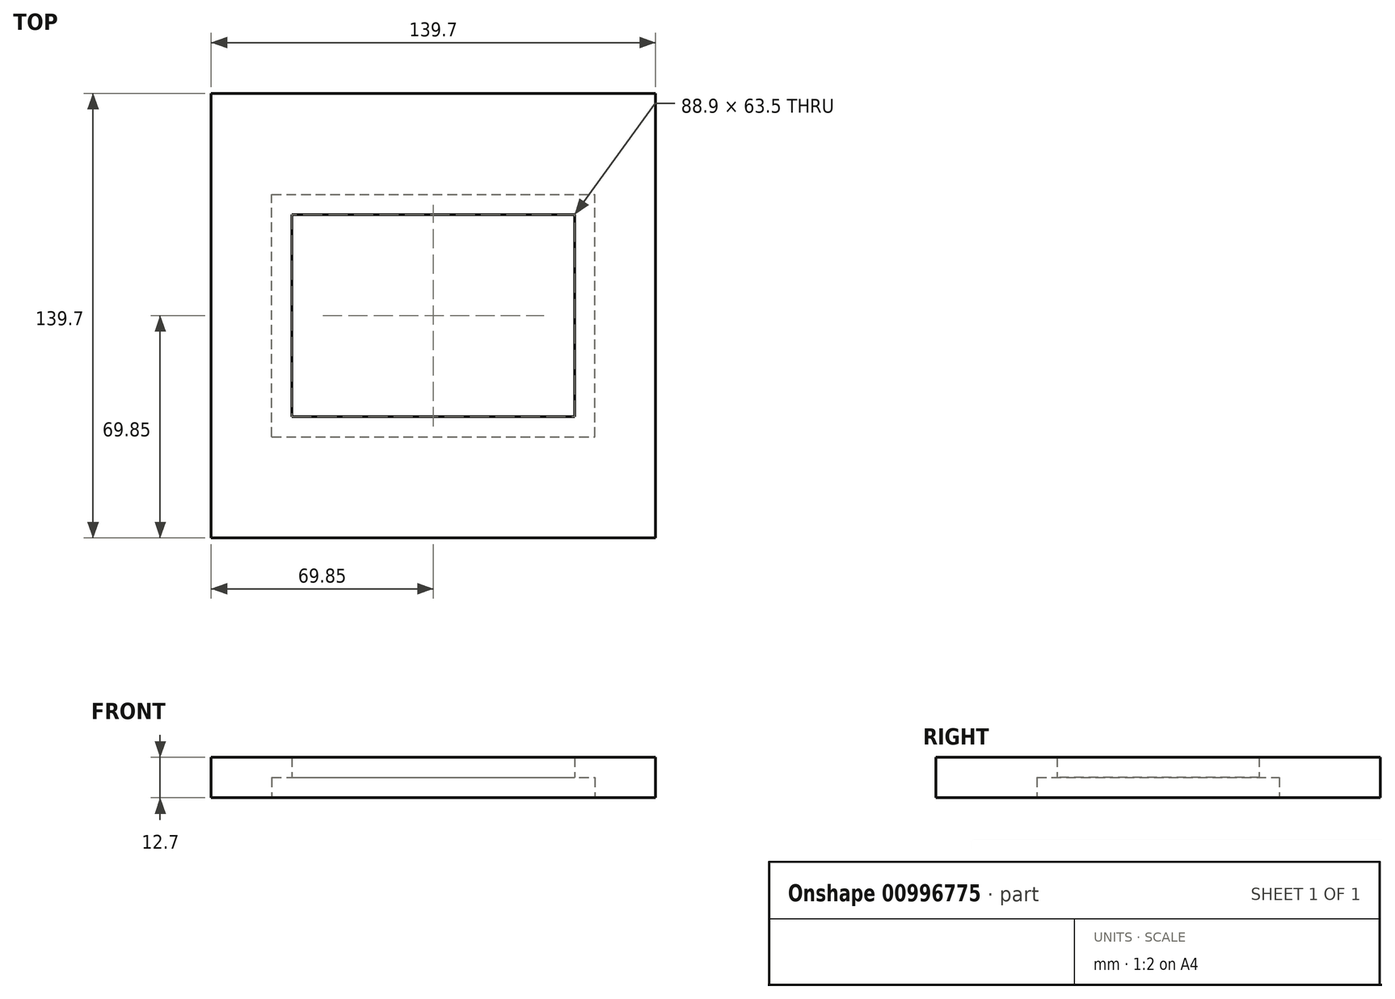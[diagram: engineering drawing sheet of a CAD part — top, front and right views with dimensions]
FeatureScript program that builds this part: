
annotation { "Feature Type Name" : "Feature", "Feature Type Description" : "" }
export const myFeature = defineFeature(function(context is Context, id is Id, definition is map)
    precondition{}
    {
        {
            var Q0;
            Q0=qCreatedBy(makeId("Top.planeOp"),FACE);
            var sketch = newSketch(context, id + "F0", { "sketchPlane" : qUnion([Q0])});
            skLineSegment(sketch, "E0.bottom", {"start": v(-50.8, -38.1) * mm, "end": v(50.8, -38.1) * mm});
            skLineSegment(sketch, "E0.top", {"start": v(-50.8, 38.1) * mm, "end": v(50.8, 38.1) * mm});
            skLineSegment(sketch, "E0.left", {"start": v(-50.8, -38.1) * mm, "end": v(-50.8, 38.1) * mm});
            skLineSegment(sketch, "E0.right", {"start": v(50.8, -38.1) * mm, "end": v(50.8, 38.1) * mm});
            skLineSegment(sketch, "E1", {"start": v(-50.8, 0) * mm, "end": v(50.8, 0) * mm, "construction": true});
            skLineSegment(sketch, "E2", {"start": v(0, 38.1) * mm, "end": v(0, -38.1) * mm, "construction": true});
            skSolve(sketch);
        }
        {
            var Q0;
            Q0=qCreatedBy(makeId("Top.planeOp"),FACE);
            var sketch = newSketch(context, id + "F1", { "sketchPlane" : qUnion([Q0])});
            skLineSegment(sketch, "E3.bottom", {"start": v(-95.25, 95.25) * mm, "end": v(95.25, 95.25) * mm});
            skLineSegment(sketch, "E3.top", {"start": v(-95.25, -95.25) * mm, "end": v(95.25, -95.25) * mm});
            skLineSegment(sketch, "E3.left", {"start": v(-95.25, 95.25) * mm, "end": v(-95.25, -95.25) * mm});
            skLineSegment(sketch, "E3.right", {"start": v(95.25, 95.25) * mm, "end": v(95.25, -95.25) * mm});
            skPoint(sketch, "E3.middle", {"position": v(0, 0) * mm});
            skSolve(sketch);
        }
        {
            var Q0;
            Q0=makeQuery(id+"F1.imprint","IMPRINT",FACE,{"disambiguationData":[TD([[makeQuery(id+"F1.imprint","IMPRINT",EDGE,{"derivedFrom":sQuery(id+"F1.wireOp",EDGE,"E3.bottom")}),-1.0]])]});
            var sketch = newSketch(context, id + "F2", { "sketchPlane" : qUnion([Q0])});
            skLineSegment(sketch, "E4.bottom", {"start": v(-69.85, 69.85) * mm, "end": v(69.85, 69.85) * mm});
            skLineSegment(sketch, "E4.top", {"start": v(-69.85, -69.85) * mm, "end": v(69.85, -69.85) * mm});
            skLineSegment(sketch, "E4.left", {"start": v(-69.85, 69.85) * mm, "end": v(-69.85, -69.85) * mm});
            skLineSegment(sketch, "E4.right", {"start": v(69.85, 69.85) * mm, "end": v(69.85, -69.85) * mm});
            skPoint(sketch, "E4.middle", {"position": v(0, 0) * mm});
            skLineSegment(sketch, "E5.bottom", {"start": v(-44.45, 31.75) * mm, "end": v(44.45, 31.75) * mm});
            skLineSegment(sketch, "E5.top", {"start": v(-44.45, -31.75) * mm, "end": v(44.45, -31.75) * mm});
            skLineSegment(sketch, "E5.left", {"start": v(-44.45, 31.75) * mm, "end": v(-44.45, -31.75) * mm});
            skLineSegment(sketch, "E5.right", {"start": v(44.45, 31.75) * mm, "end": v(44.45, -31.75) * mm});
            skSolve(sketch);
        }
        {
            var Q0;
            Q0 = qSketchRegion(id + "F2", true);
            extrude(context, id + "F3", {"entities" : qUnion([Q0]), "depth" : 12.7 * mm, "offsetDistance" : 25.4 * mm});
        }
        {
            var Q0;
            Q0 = qSketchRegion(id + "F0", true);
            extrude(context, id + "F4", {"entities" : qUnion([Q0]), "operationType" : NewBodyOperationType.REMOVE, "depth" : 6.35 * mm, "offsetDistance" : 25.4 * mm});
        }
    });
